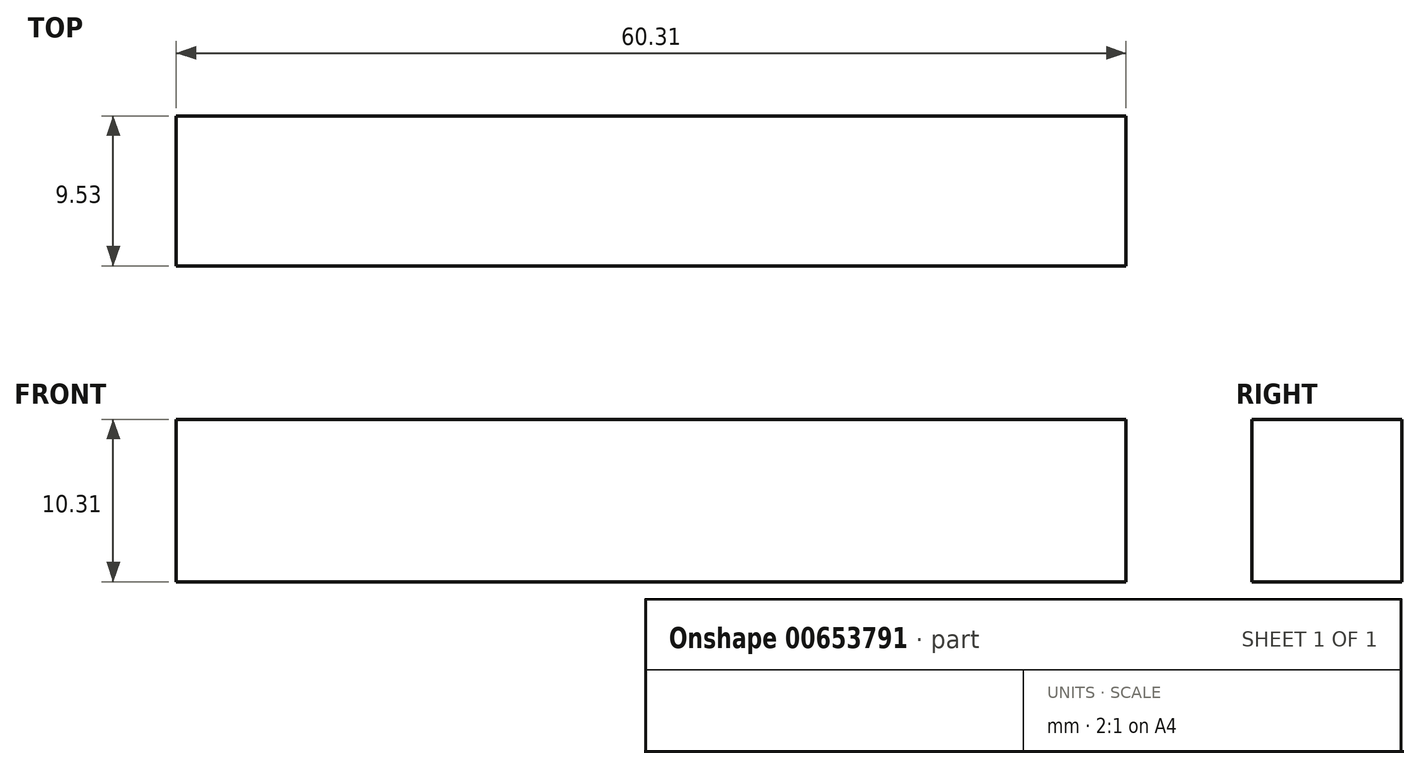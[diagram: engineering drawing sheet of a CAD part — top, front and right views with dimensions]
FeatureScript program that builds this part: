
annotation { "Feature Type Name" : "Feature", "Feature Type Description" : "" }
export const myFeature = defineFeature(function(context is Context, id is Id, definition is map)
    precondition{}
    {
        {
            var Q0;
            Q0=qCreatedBy(makeId("Right.planeOp"),FACE);
            var sketch = newSketch(context, id + "F0", { "sketchPlane" : qUnion([Q0])});
            skLineSegment(sketch, "E0.bottom", {"start": v(0, 0) * mm, "end": v(9.53, 0) * mm});
            skLineSegment(sketch, "E0.top", {"start": v(0, 10.31) * mm, "end": v(9.52, 10.31) * mm});
            skLineSegment(sketch, "E0.left", {"start": v(0, 0) * mm, "end": v(0, 10.31) * mm});
            skLineSegment(sketch, "E0.right", {"start": v(9.53, 0) * mm, "end": v(9.52, 10.31) * mm});
            skSolve(sketch);
        }
        {
            var Q0;
            Q0 = qSketchRegion(id + "F0", true);
            extrude(context, id + "F1", {"entities" : qUnion([Q0]), "depth" : 30.16 * mm, "offsetDistance" : 25.4 * mm, "hasSecondDirection" : true, "secondDirectionOppositeDirection" : true, "secondDirectionDepth" : 30.15 * mm});
        }
    });
